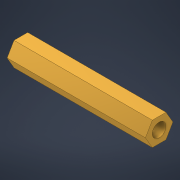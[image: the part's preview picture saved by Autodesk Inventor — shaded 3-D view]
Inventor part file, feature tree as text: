
AUTODESK INVENTOR PART (.ipt)
format: ipt  version: 2022 (Build 260153000, 153)  size: 97,280 bytes
history: native  units: mm
features: extrude x1, sketch x1
ambient origin geometry x8: Origin, YZ Plane, XZ Plane, XY Plane, X Axis, Y Axis, Z Axis, Center Point
bodies: Solid1 (feature_tree)
feature tree (2):
  extrude  "Extrusion1"  Depth=3.0mm
  sketch  "Sketch1"  dims[d0=6.0mm d1=3.0mm d2=30.296mm d3=0.0mm d4=5.196152mm]
